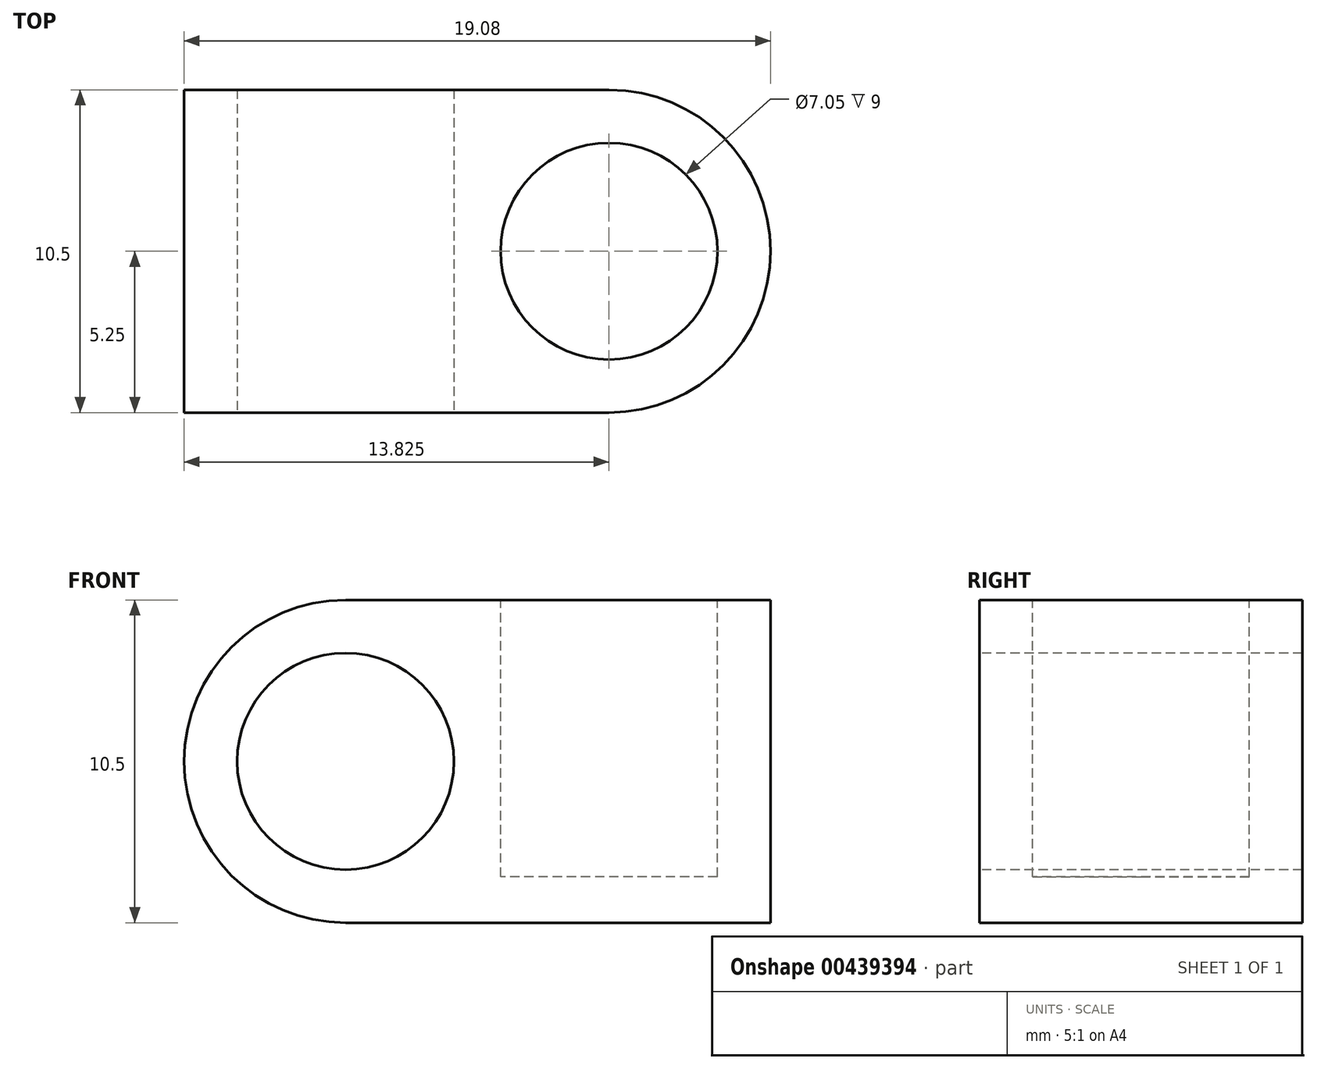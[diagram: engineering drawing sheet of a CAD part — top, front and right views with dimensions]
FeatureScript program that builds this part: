
annotation { "Feature Type Name" : "Feature", "Feature Type Description" : "" }
export const myFeature = defineFeature(function(context is Context, id is Id, definition is map)
    precondition{}
    {
        {
            var Q0;
            Q0=qCreatedBy(makeId("Front.planeOp"),FACE);
            var sketch = newSketch(context, id + "F0", { "sketchPlane" : qUnion([Q0])});
            skLineSegment(sketch, "E0.bottom", {"start": v(-9.53, 5.25) * mm, "end": v(9.54, 5.25) * mm});
            skLineSegment(sketch, "E0.top", {"start": v(-9.54, -5.25) * mm, "end": v(9.53, -5.25) * mm});
            skLineSegment(sketch, "E0.left", {"start": v(-9.53, 5.25) * mm, "end": v(-9.54, -5.25) * mm});
            skLineSegment(sketch, "E0.right", {"start": v(9.54, 5.25) * mm, "end": v(9.53, -5.25) * mm});
            skLineSegment(sketch, "E1", {"start": v(-9.54, 5.25) * mm, "end": v(9.54, -5.25) * mm, "construction": true});
            skLineSegment(sketch, "E2", {"start": v(9.54, 5.25) * mm, "end": v(-9.54, -5.25) * mm, "construction": true});
            skSolve(sketch);
        }
        {
            var Q0;
            Q0 = qSketchRegion(id + "F0", true);
            extrude(context, id + "F1", {"entities" : qUnion([Q0]), "oppositeDirection" : true, "depth" : 10.5 * mm});
        }
        {
            var Q0;
            Q0=makeQuery(id+"F1.opExtrude","CAP_FACE",FACE,{"disambiguationData":[OSD([sQuery(id+"F0.wireOp",EDGE,"E0.bottom"),sQuery(id+"F0.wireOp",EDGE,"E0.top"),sQuery(id+"F0.wireOp",EDGE,"E0.left"),sQuery(id+"F0.wireOp",EDGE,"E0.right")])],"isStart":true});
            var sketch = newSketch(context, id + "F2", { "sketchPlane" : qUnion([Q0])});
            skArc(sketch, "E3", {"start": v(-4.28, 5.25) * mm, "mid": v(-9.53, 0) * mm, "end": v(-4.29, -5.25) * mm});
            skCircle(sketch, "E4", {"center": v(-4.28, 0) * mm, "radius": 3.52 * mm});
            skLineSegment(sketch, "E5.0", {"start": v(-9.53, 5.25) * mm, "end": v(-4.28, 5.25) * mm});
            skLineSegment(sketch, "E6.0", {"start": v(-9.53, 5.25) * mm, "end": v(-9.54, -5.25) * mm});
            skLineSegment(sketch, "E7.0", {"start": v(-9.54, -5.25) * mm, "end": v(-4.28, -5.25) * mm});
            skPoint(sketch, "E8.orphan", {"position": v(9.54, 5.25) * mm});
            skPoint(sketch, "E9.orphan", {"position": v(9.53, -5.25) * mm});
            skSolve(sketch);
        }
        {
            var Q0;
            Q0 = qSketchRegion(id + "F2", true);
            extrude(context, id + "F3", {"entities" : qUnion([Q0]), "operationType" : NewBodyOperationType.REMOVE, "endBound" : BoundingType.UP_TO_NEXT, "oppositeDirection" : true, "depth" : 25 * mm});
        }
        {
            var Q0;
            Q0=makeQuery(id+"F1.opExtrude","SWEPT_FACE",FACE,{"disambiguationData":[OSD([sQuery(id+"F0.wireOp",EDGE,"E0.bottom")])]});
            var sketch = newSketch(context, id + "F4", { "sketchPlane" : qUnion([Q0])});
            skCircle(sketch, "E10", {"center": v(4.29, 5.25) * mm, "radius": 3.52 * mm});
            skPoint(sketch, "E11.orphan", {"position": v(-4.28, 10.5) * mm});
            skPoint(sketch, "E12.orphan", {"position": v(-4.28, 0) * mm});
            skPoint(sketch, "E13.orphan", {"position": v(9.54, 10.5) * mm});
            skPoint(sketch, "E14.0.end.orphan", {"position": v(9.54, 0) * mm});
            skCircle(sketch, "E15", {"center": v(4.29, 5.25) * mm, "radius": 5.25 * mm, "construction": true});
            skSolve(sketch);
        }
        {
            var Q0;
            Q0 = qSketchRegion(id + "F4", true);
            extrude(context, id + "F5", {"entities" : qUnion([Q0]), "operationType" : NewBodyOperationType.REMOVE, "oppositeDirection" : true, "depth" : 9 * mm});
        }
        {
            var Q0;
            Q0=makeQuery(id+"F1.opExtrude","SWEPT_FACE",FACE,{"disambiguationData":[OSD([sQuery(id+"F0.wireOp",EDGE,"E0.bottom")])]});
            var sketch = newSketch(context, id + "F6", { "sketchPlane" : qUnion([Q0])});
            skArc(sketch, "E16.0", {"start": v(4.28, 0) * mm, "mid": v(9.54, 5.25) * mm, "end": v(4.29, 10.5) * mm});
            skLineSegment(sketch, "E17.0", {"start": v(4.28, 10.5) * mm, "end": v(9.54, 10.5) * mm});
            skLineSegment(sketch, "E18.0", {"start": v(9.54, 10.5) * mm, "end": v(9.54, 0) * mm});
            skLineSegment(sketch, "E19.0", {"start": v(4.28, 0) * mm, "end": v(9.54, 0) * mm});
            skPoint(sketch, "E20.orphan", {"position": v(-4.28, 10.5) * mm});
            skPoint(sketch, "E21.orphan", {"position": v(-4.28, 0) * mm});
            skSolve(sketch);
        }
        {
            var Q0;
            Q0 = qSketchRegion(id + "F6", true);
            extrude(context, id + "F7", {"entities" : qUnion([Q0]), "operationType" : NewBodyOperationType.REMOVE, "endBound" : BoundingType.THROUGH_ALL, "oppositeDirection" : true, "depth" : 25 * mm});
        }
    });
